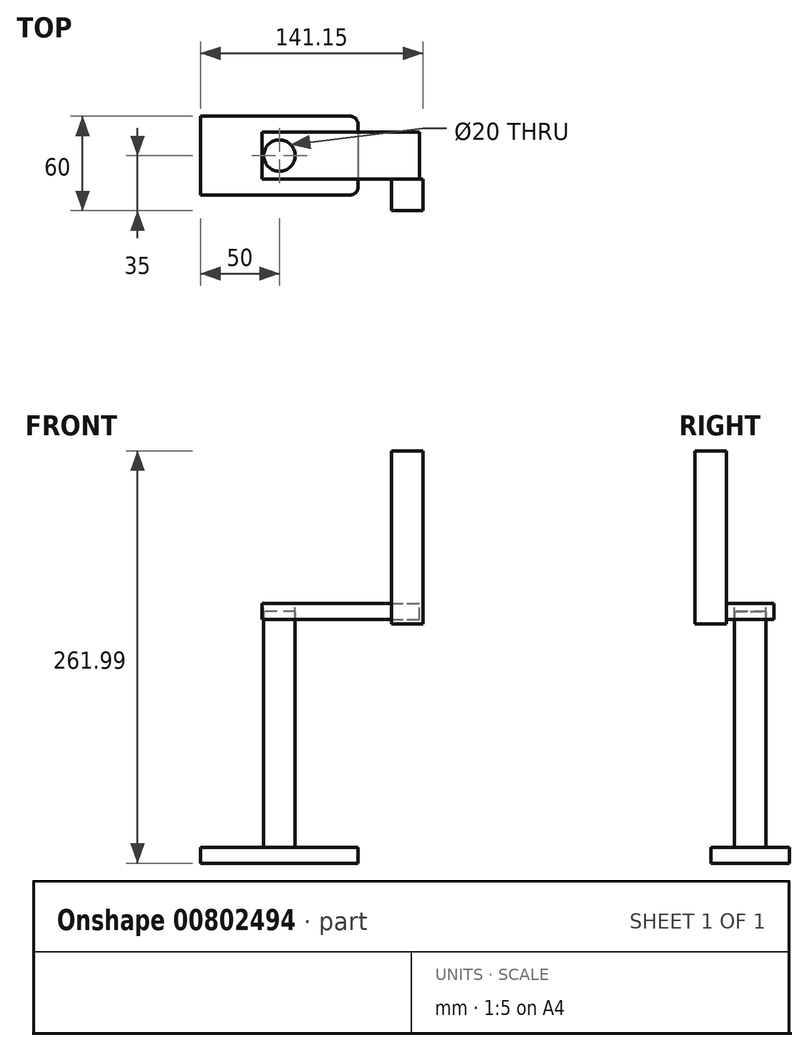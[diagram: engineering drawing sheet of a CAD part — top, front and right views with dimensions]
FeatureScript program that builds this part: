
annotation { "Feature Type Name" : "Feature", "Feature Type Description" : "" }
export const myFeature = defineFeature(function(context is Context, id is Id, definition is map)
    precondition{}
    {
        {
            var Q0;
            Q0=qCreatedBy(makeId("Top.planeOp"),FACE);
            var sketch = newSketch(context, id + "F0", { "sketchPlane" : qUnion([Q0])});
            skLineSegment(sketch, "E0.bottom", {"start": v(-50, 25) * mm, "end": v(50, 25) * mm});
            skLineSegment(sketch, "E0.top", {"start": v(-50, -25) * mm, "end": v(50, -25) * mm});
            skLineSegment(sketch, "E0.left", {"start": v(-50, 25) * mm, "end": v(-50, -25) * mm});
            skLineSegment(sketch, "E0.right", {"start": v(50, 25) * mm, "end": v(50, -25) * mm});
            skSolve(sketch);
        }
        {
            var Q0;
            Q0=makeQuery(id+"F0.imprint","IMPRINT",FACE,{"disambiguationData":[TD([[makeQuery(id+"F0.imprint","IMPRINT",EDGE,{"derivedFrom":sQuery(id+"F0.wireOp",EDGE,"E0.bottom")}),-1.0]])]});
            extrude(context, id + "F1", {"entities" : qUnion([Q0]), "depth" : 10 * mm, "offsetDistance" : 25 * mm});
        }
        {
            var Q0;
            Q0=makeQuery(id+"F1.opExtrude","SWEPT_EDGE",EDGE,{"disambiguationData":[OSD([sQuery(id+"F0.wireOp",EDGE,"E0.top"),sQuery(id+"F0.wireOp",EDGE,"E0.right")])]});
            fillet(context, id + "F2", {"entities" : qUnion([Q0]), "radius" : 5 * mm, "tangentPropagation" : true, "allowEdgeOverflow" : false});
        }
        {
            var Q0;
            Q0=makeQuery(id+"F1.opExtrude","SWEPT_EDGE",EDGE,{"disambiguationData":[OSD([sQuery(id+"F0.wireOp",EDGE,"E0.bottom"),sQuery(id+"F0.wireOp",EDGE,"E0.right")])]});
            fillet(context, id + "F3", {"entities" : qUnion([Q0]), "radius" : 5 * mm, "tangentPropagation" : true, "allowEdgeOverflow" : false});
        }
        {
            var Q0;
            Q0=makeQuery(id+"F1.opExtrude","CAP_FACE",FACE,{"disambiguationData":[OSD([sQuery(id+"F0.wireOp",EDGE,"E0.bottom"),sQuery(id+"F0.wireOp",EDGE,"E0.top"),sQuery(id+"F0.wireOp",EDGE,"E0.left"),sQuery(id+"F0.wireOp",EDGE,"E0.right")])],"isStart":false});
            var sketch = newSketch(context, id + "F4", { "sketchPlane" : qUnion([Q0])});
            skCircle(sketch, "E1", {"center": v(0, 0) * mm, "radius": 10 * mm});
            skSolve(sketch);
        }
        {
            var Q0;
            Q0=makeQuery(id+"F4.imprint","IMPRINT",FACE,{"disambiguationData":[TD([[makeQuery(id+"F4.imprint","IMPRINT",EDGE,{"derivedFrom":sQuery(id+"F4.wireOp",EDGE,"E1")}),1.0]])]});
            extrude(context, id + "F5", {"entities" : qUnion([Q0]), "depth" : 150 * mm, "offsetDistance" : 25 * mm});
        }
        {
            var Q0;
            Q0=makeQuery(id+"F5.opExtrude","CAP_FACE",FACE,{"disambiguationData":[OSD([sQuery(id+"F4.wireOp",EDGE,"E1")])],"isStart":false});
            var sketch = newSketch(context, id + "F6", { "sketchPlane" : qUnion([Q0])});
            skLineSegment(sketch, "E2.bottom", {"start": v(-11, 15) * mm, "end": v(89, 15) * mm});
            skLineSegment(sketch, "E2.top", {"start": v(-11, -15) * mm, "end": v(89, -15) * mm});
            skLineSegment(sketch, "E2.left", {"start": v(-11, 15) * mm, "end": v(-11, -15) * mm});
            skLineSegment(sketch, "E2.right", {"start": v(89, 15) * mm, "end": v(89, -15) * mm});
            skLineSegment(sketch, "E3", {"start": v(-11, 0) * mm, "end": v(89, 0) * mm, "construction": true});
            skCircle(sketch, "E4.0.0", {"center": v(0, 0) * mm, "radius": 10 * mm});
            skSolve(sketch);
        }
        {
            var Q0;
            Q0=makeQuery(id+"F6.imprint","IMPRINT",FACE,{"disambiguationData":[TD([[makeQuery(id+"F6.imprint","IMPRINT",EDGE,{"derivedFrom":sQuery(id+"F6.wireOp",EDGE,"E2.bottom")}),-1.0]])]});
            extrude(context, id + "F7", {"entities" : qUnion([Q0]), "endBound" : BoundingType.SYMMETRIC, "oppositeDirection" : true, "depth" : 10 * mm, "offsetDistance" : 25 * mm});
        }
        {
            var Q0;
            Q0=makeQuery(id+"F7.opExtrude","SWEPT_FACE",FACE,{"disambiguationData":[OSD([sQuery(id+"F6.wireOp",EDGE,"E2.top")])]});
            var sketch = newSketch(context, id + "F8", { "sketchPlane" : qUnion([Q0])});
            skLineSegment(sketch, "E5.bottom", {"start": v(71.15, 261.99) * mm, "end": v(91.15, 261.99) * mm});
            skLineSegment(sketch, "E5.top", {"start": v(71.15, 151.99) * mm, "end": v(91.15, 151.99) * mm});
            skLineSegment(sketch, "E5.left", {"start": v(71.15, 261.99) * mm, "end": v(71.15, 151.99) * mm});
            skLineSegment(sketch, "E5.right", {"start": v(91.15, 261.99) * mm, "end": v(91.15, 151.99) * mm});
            skSolve(sketch);
        }
        {
            var Q0;
            Q0 = qSketchRegion(id + "F8", true);
            extrude(context, id + "F9", {"entities" : qUnion([Q0]), "depth" : 20 * mm, "offsetDistance" : 25 * mm});
        }
    });
